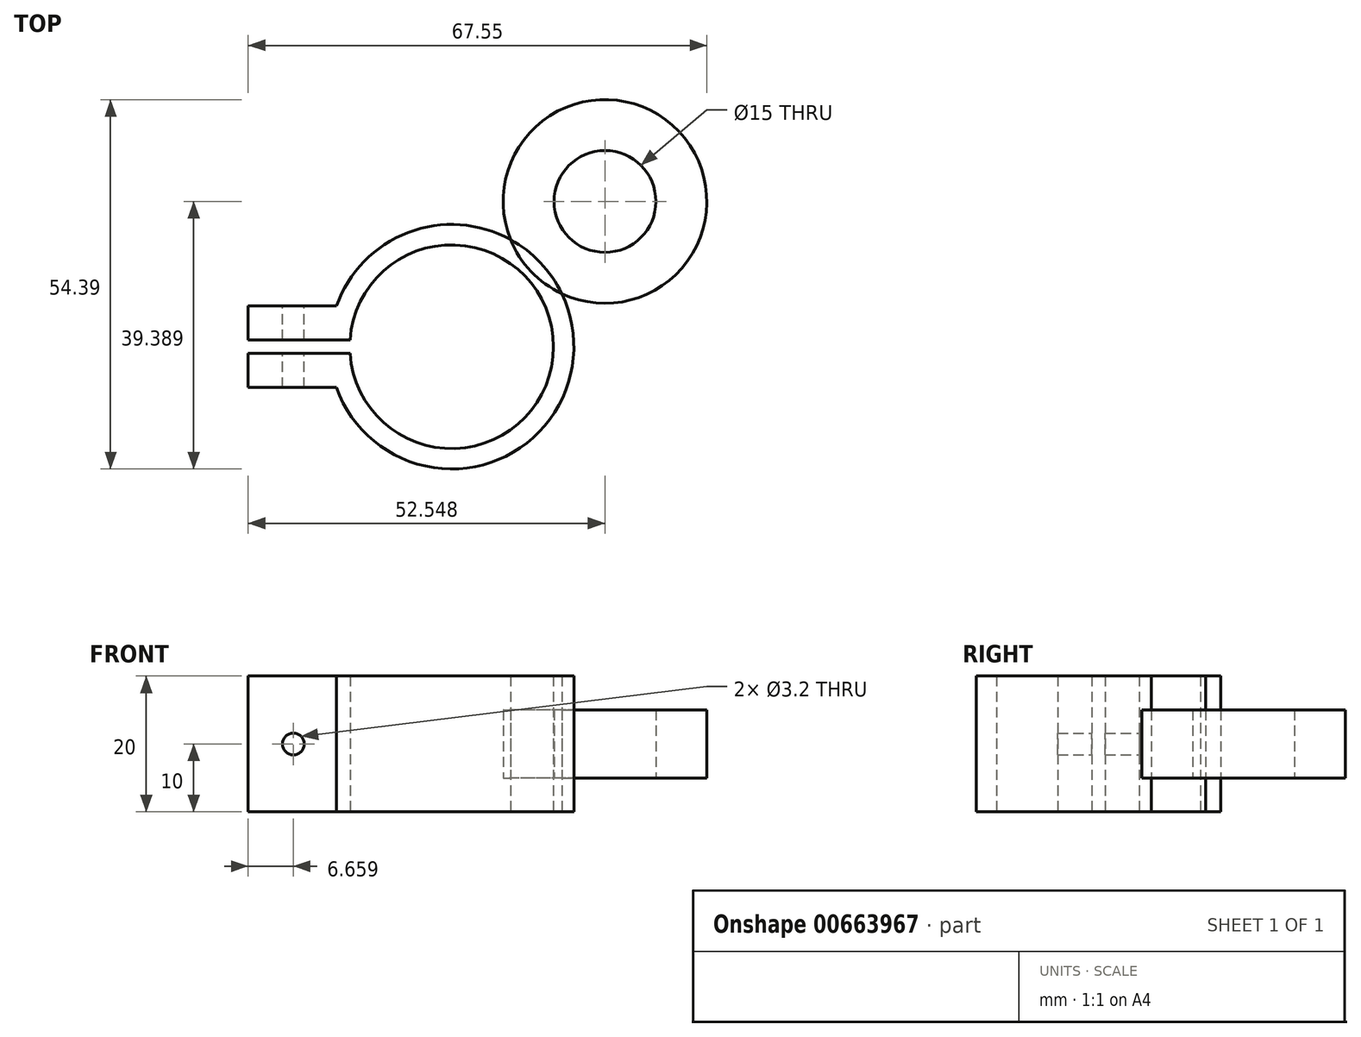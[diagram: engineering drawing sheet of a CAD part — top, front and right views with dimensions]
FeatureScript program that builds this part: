
annotation { "Feature Type Name" : "Feature", "Feature Type Description" : "" }
export const myFeature = defineFeature(function(context is Context, id is Id, definition is map)
    precondition{}
    {
        {
            var Q0;
            Q0=qCreatedBy(makeId("Top.planeOp"),FACE);
            var sketch = newSketch(context, id + "F0", { "sketchPlane" : qUnion([Q0])});
            skEllipticalArc(sketch, "E0", {});
            skArc(sketch, "E1", {"start": v(-16.97, -6) * mm, "mid": v(18, 0) * mm, "end": v(-16.97, 6) * mm});
            skPoint(sketch, "E2.start.orphan", {"position": v(-15, 0) * mm});
            skLineSegment(sketch, "E3.bottom", {"start": v(-14.97, 1) * mm, "end": v(-29.97, 1) * mm});
            skLineSegment(sketch, "E3.top", {"start": v(-16.97, 6) * mm, "end": v(-29.97, 6) * mm});
            skLineSegment(sketch, "E3.right", {"start": v(-29.97, 1) * mm, "end": v(-29.97, 6) * mm});
            skLineSegment(sketch, "E4.bottom", {"start": v(-14.97, -1) * mm, "end": v(-29.97, -1) * mm});
            skLineSegment(sketch, "E4.top", {"start": v(-16.97, -6) * mm, "end": v(-29.97, -6) * mm});
            skLineSegment(sketch, "E4.right", {"start": v(-29.97, -1) * mm, "end": v(-29.97, -6) * mm});
            skLineSegment(sketch, "E5", {"start": v(-14.97, 1) * mm, "end": v(-14.97, 1) * mm});
            skLineSegment(sketch, "E6", {"start": v(-14.97, -1) * mm, "end": v(-14.97, -1) * mm});
            skEllipse(sketch, "E7", {"center": v(22.58, 21.39) * mm, "majorRadius": 7.5 * mm, "minorRadius": 7.5 * mm, "majorAxis": v(-0.78, -0.62)});
            skCircle(sketch, "E8", {"center": v(22.58, 21.39) * mm, "radius": 15 * mm});
            skCircle(sketch, "E9", {"center": v(22.58, 21.39) * mm, "radius": 10 * mm});
            const initialGuessF0  = {"E0": [0, 0, -0.549177872152529, -0.8357054892353051, 0.015, 0.015, 5.360485295239263, 5.227052998418813]};
            skSetInitialGuess(sketch, initialGuessF0);
            skSolve(sketch);
        }
        {
            var Q0;
            Q0=makeQuery(id+"F0.imprint","IMPRINT",FACE,{"disambiguationData":[TD([[makeQuery(id+"F0.imprint","IMPRINT",EDGE,{"derivedFrom":sQuery(id+"F0.wireOp",EDGE,"E0")}),-1.0]])]});
            extrude(context, id + "F1", {"entities" : qUnion([Q0]), "depth" : 10 * mm, "offsetDistance" : 25 * mm, "hasSecondDirection" : true, "secondDirectionOppositeDirection" : true, "secondDirectionDepth" : 10 * mm});
        }
        {
            var Q0;
            {var subQ0=sQuery(id+"F0.wireOp",EDGE,"E8");var subQ1=sQuery(id+"F0.wireOp",EDGE,"E1");var subQ2=makeQuery(id+"F0.imprint","INTERSECT",VERTEX,{"disambiguationData":[OD(0.0)],"derivedFrom":[subQ1,subQ0]});Q0=makeQuery(id+"F0.imprint","IMPRINT",FACE,{"disambiguationData":[TD([[makeQuery(id+"F0.imprint","IMPRINT",EDGE,{"disambiguationData":[TD([[subQ2,-1.0]])],"derivedFrom":subQ1}),1.0]])]});}
            extrude(context, id + "F2", {"entities" : qUnion([Q0]), "operationType" : NewBodyOperationType.ADD, "depth" : 5 * mm, "offsetDistance" : 25 * mm, "hasSecondDirection" : true, "secondDirectionOppositeDirection" : true, "secondDirectionDepth" : 5 * mm});
        }
        {
            var Q0;
            Q0=makeQuery(id+"F0.imprint","IMPRINT",FACE,{"disambiguationData":[TD([[makeQuery(id+"F0.imprint","IMPRINT",EDGE,{"derivedFrom":sQuery(id+"F0.wireOp",EDGE,"E9")}),-1.0]])]});
            var Q1;
            Q1=makeQuery(id+"F0.imprint","IMPRINT",FACE,{"disambiguationData":[TD([[makeQuery(id+"F0.imprint","IMPRINT",EDGE,{"derivedFrom":sQuery(id+"F0.wireOp",EDGE,"E7")}),-1.0]])]});
            extrude(context, id + "F3", {"entities" : qUnion([Q0, Q1]), "operationType" : NewBodyOperationType.ADD, "depth" : 5 * mm, "offsetDistance" : 25 * mm, "hasSecondDirection" : true, "secondDirectionOppositeDirection" : true, "secondDirectionDepth" : 5 * mm});
        }
        {
            var Q0;
            Q0=makeQuery(id+"F1.opExtrude","SWEPT_FACE",FACE,{"disambiguationData":[OSD([sQuery(id+"F0.wireOp",EDGE,"E3.top")])]});
            var sketch = newSketch(context, id + "F4", { "sketchPlane" : qUnion([Q0])});
            skEllipse(sketch, "E10", {"center": v(23.31, 0) * mm, "majorRadius": 1.6 * mm, "minorRadius": 1.6 * mm, "majorAxis": v(0, -1)});
            skSolve(sketch);
        }
        {
            var Q0;
            Q0 = qSketchRegion(id + "F4", true);
            extrude(context, id + "F5", {"entities" : qUnion([Q0]), "operationType" : NewBodyOperationType.REMOVE, "oppositeDirection" : true, "depth" : 25 * mm, "offsetDistance" : 25 * mm});
        }
    });
